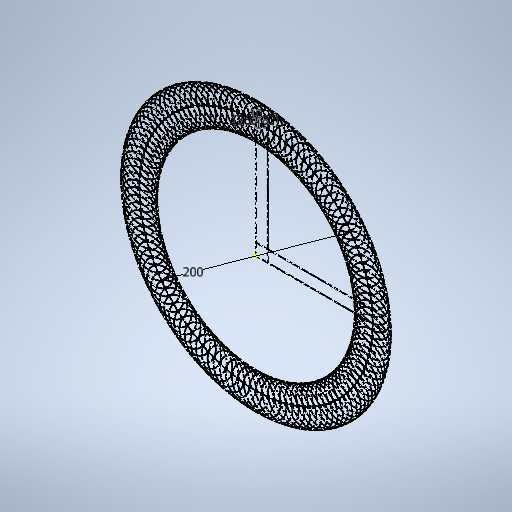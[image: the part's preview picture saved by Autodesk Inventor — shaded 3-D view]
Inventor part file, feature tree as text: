
AUTODESK INVENTOR PART (.ipt)
format: ipt  version: 2025.2 (Build 292293000, 293)  size: 337,408 bytes
history: native  units: mm
features: sketch x8
ambient origin geometry x8: Origin, YZ Plane, XZ Plane, XY Plane, X Axis, Y Axis, Z Axis, Center Point
feature tree (8):
  sketch  "Sketch1"  dims[d0=10.0mm]
  sketch  "Sketch3"  dims[d4=25.0mm]
  sketch  "Sketch4"  dims[d5=50.0mm]
  sketch  "Sketch5"  dims[d6=200.0mm]
  sketch  "Sketch6"  dims[d7=60.0mm d9=360.0deg d11=1200.0mm d13=360.0deg d15=20.0mm d17=10.0mm d18=20.0mm d20=10.0mm]
  sketch  "Sketch Circular Pattern1"  dims[d1=50.0mm]
  sketch  "Sketch Circular Pattern2"  dims[d3=50.0mm]
  sketch  "Sketch Rectangular Pattern1"  dims[d2=8.884938mm]
